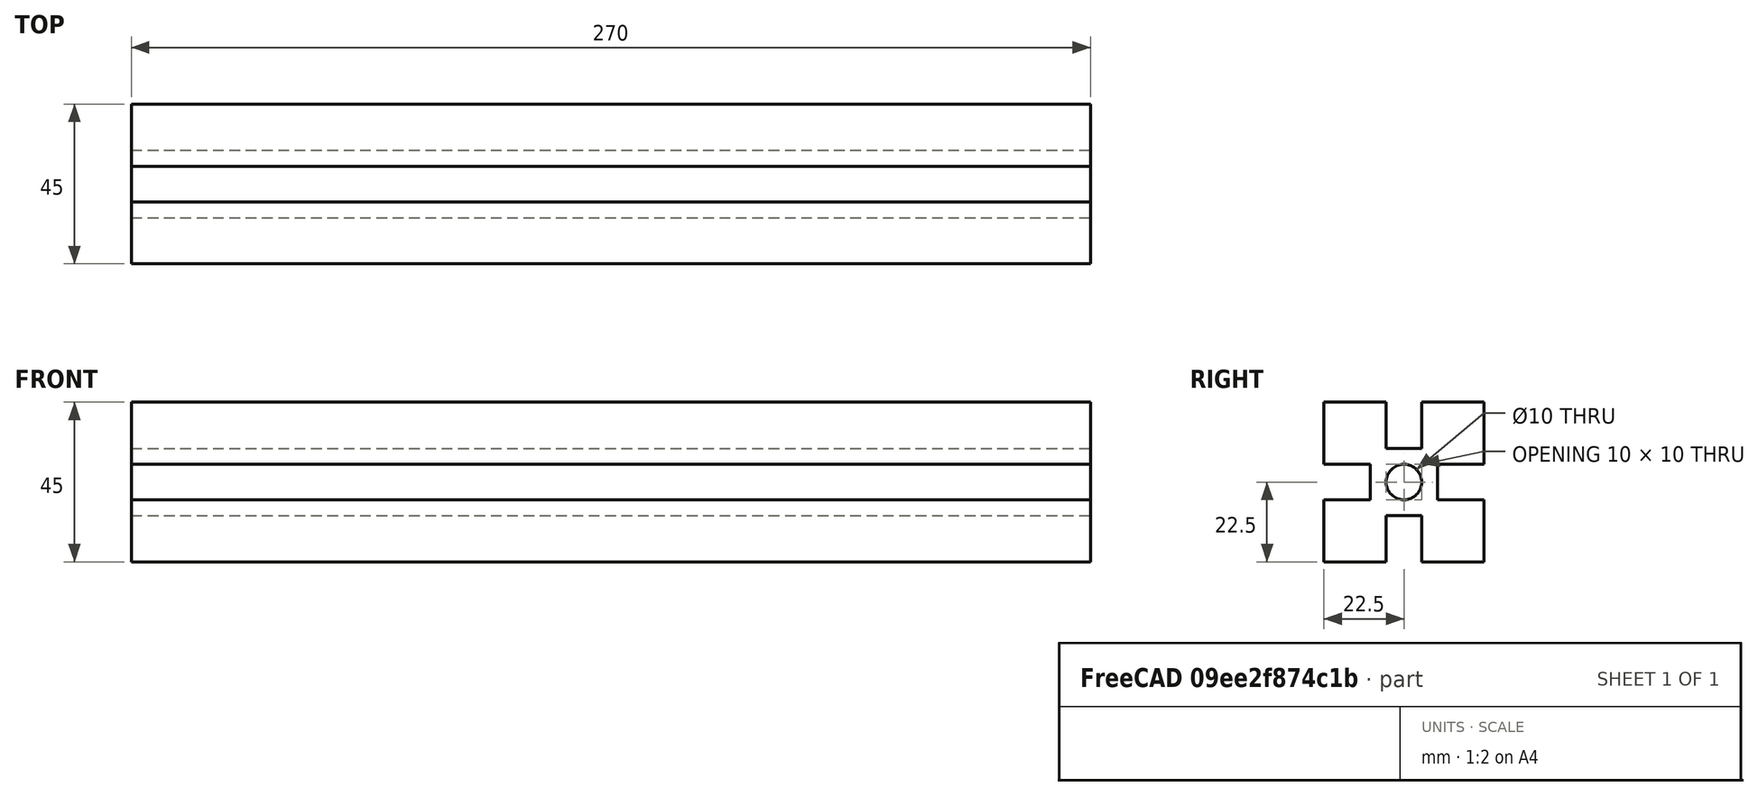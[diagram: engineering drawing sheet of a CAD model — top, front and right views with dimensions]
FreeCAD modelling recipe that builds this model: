
FCSTD DOCUMENT  (FreeCAD 1.0R39109 (Git))
Label: vslot 45x45x270
License: All rights reserved
LicenseURL: https://en.wikipedia.org/wiki/All_rights_reserved
objects: PartDesign::Pocket×2, Part::Feature×1, PartDesign::FeatureBase×1, PartDesign::Body×1
note: 10 computed .brp shape members not serialized (recipe doc carries the construction recipe); baked Part::Feature solids carry a one-line shape summary decoded from their .brp

FEATURE [Part::Feature] Part__Feature  label="1"
  shape: bbox 1000 x 45 x 45 mm, 24 faces (baked)
FEATURE [PartDesign::FeatureBase] BaseFeature
  BaseFeature = -> Part__Feature
  Suppressed = false
FEATURE [PartDesign::Pocket] Pocket
  BaseFeature = -> BaseFeature
  Direction = (1,0,0)
  Length = 460
  Length2 = 5
  Profile = -> BaseFeature [Face23]
  Refine = true
  Suppressed = false
  Type = 0
FEATURE [PartDesign::Pocket] Pocket001
  BaseFeature = -> Pocket
  Direction = (1,0,0)
  Length = 270
  Length2 = 5
  Profile = -> Pocket [Face1]
  Refine = true
  Suppressed = false
  Type = 0
FEATURE [PartDesign::Body] Body
  AllowCompound = false
  BaseFeature = -> Part__Feature
  Group = -> [BaseFeature,Pocket,Pocket001]
  Origin = -> Origin
  Tip = -> Pocket001
